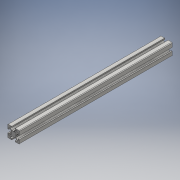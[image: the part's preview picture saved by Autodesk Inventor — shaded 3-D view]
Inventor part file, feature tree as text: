
AUTODESK INVENTOR PART (.ipt)
format: ipt  version: 2016 (Build 200138000, 138)  size: 174,080 bytes
history: native  units: mm
features: other x1, extrude x1, sketch x1
ambient origin geometry x8: Origin, YZ Plane, XZ Plane, XY Plane, X Axis, Y Axis, Z Axis, Center Point
bodies: Body1 (feature_tree)
feature tree (3):
  other  "ソリッド1"
  extrude  "押し出し1"  Depth=260.0mm TaperAngle=0.0deg
  sketch  "スケッチ1"
